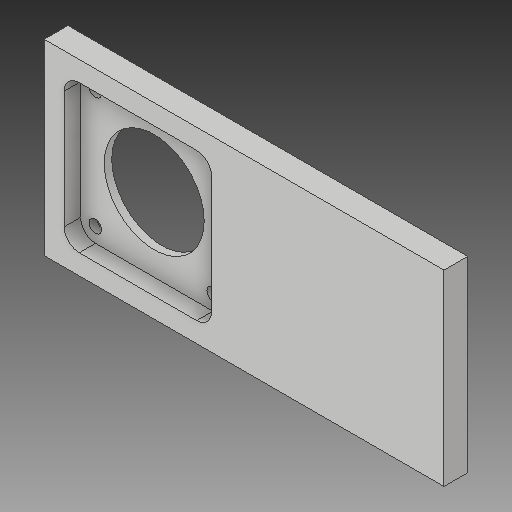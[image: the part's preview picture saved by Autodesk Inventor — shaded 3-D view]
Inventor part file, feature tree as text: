
AUTODESK INVENTOR PART (.ipt)
format: ipt  version: 2018 (Build 220112000, 112)  size: 123,904 bytes
history: native  units: mm
features: other x4, sketch x3
ambient origin geometry x8: Origin, YZ Plane, XZ Plane, XY Plane, X Axis, Y Axis, Z Axis, Center Point
bodies: Body1 (feature_tree)
feature tree (7):
  other  "SUPORTE_MOTOR_EIXO_Y_1.ipt"
  other  "Sólido1::SUPORTE_MOTOR_EIXO_Y_1.ipt"
  other  "OperaçãoIdentificador1"
  sketch  "Esboço1"  dims[d0=10.0mm]
  sketch  "Esboço9"
  sketch  "Esboço10"
  other  "Sólido1"
